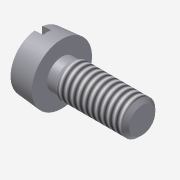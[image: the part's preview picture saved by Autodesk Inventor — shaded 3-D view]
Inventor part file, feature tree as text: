
AUTODESK INVENTOR PART (.ipt)
format: ipt  version: 2011 (Build 150239000, 239)  size: 156,672 bytes
history: native  units: mm (DEFAULTED — no unit token found)
features: extrude x1, plane x1
ambient origin geometry x7: Origin, YZ Plane, XZ Plane, X Axis, Y Axis, Z Axis, Center Point
bodies: Solid1 (feature_tree), Body (feature_tree)
feature tree (2):
  extrude  "Slot"  Depth=6.0mm
  plane  "Work Plane1"
